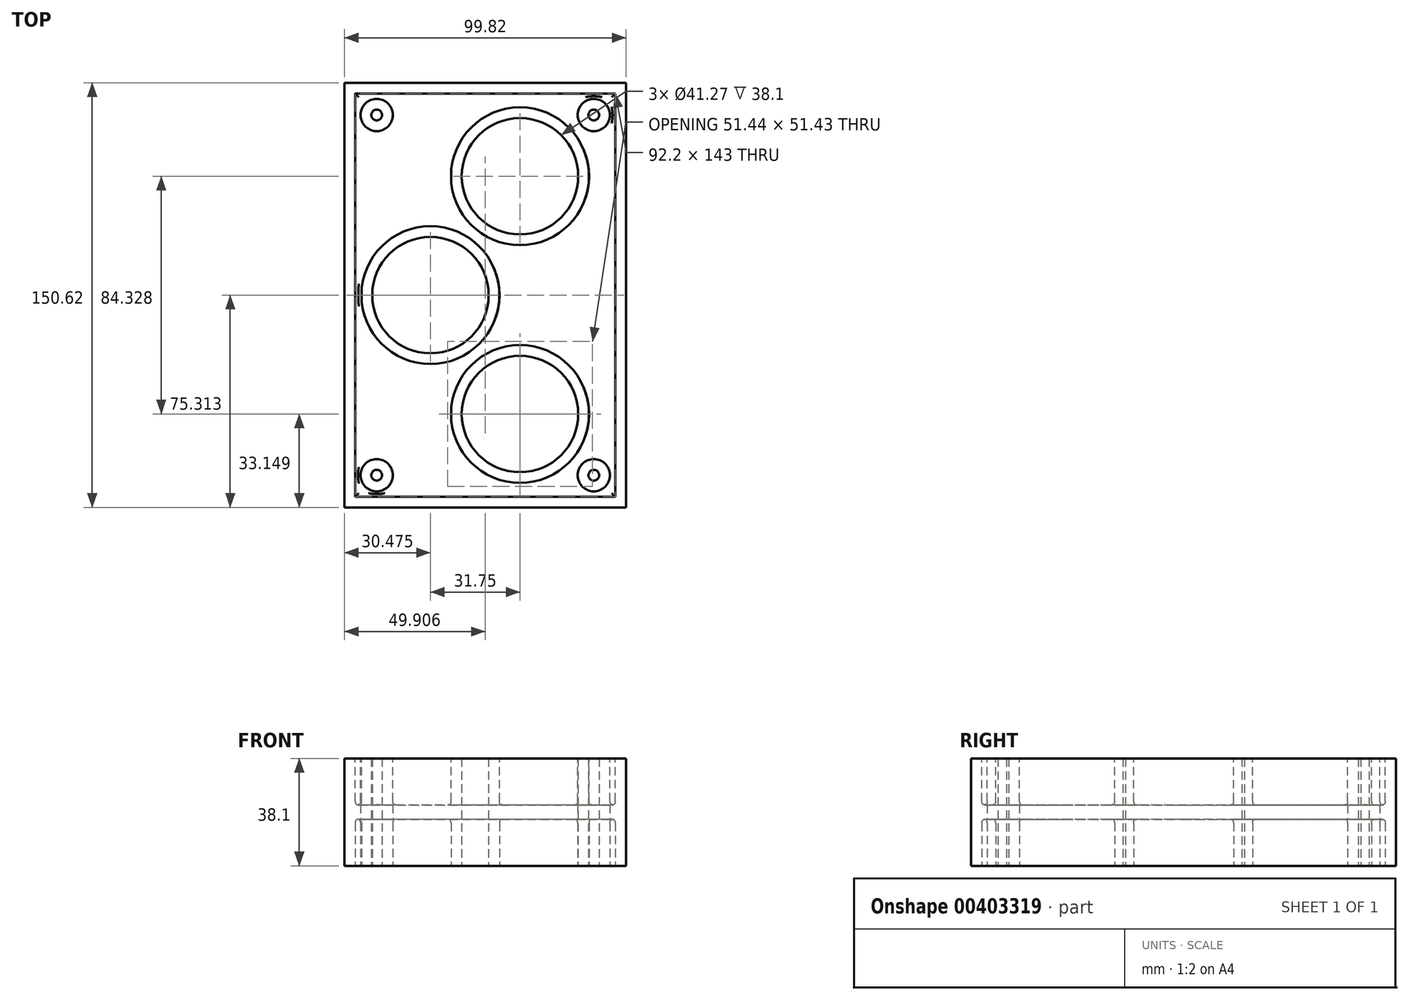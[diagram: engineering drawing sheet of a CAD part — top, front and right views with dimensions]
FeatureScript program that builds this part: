
annotation { "Feature Type Name" : "Feature", "Feature Type Description" : "" }
export const myFeature = defineFeature(function(context is Context, id is Id, definition is map)
    precondition{}
    {
        {
            var Q0;
            Q0=qCreatedBy(makeId("Top.planeOp"),FACE);
            var sketch = newSketch(context, id + "F0", { "sketchPlane" : qUnion([Q0])});
            skLineSegment(sketch, "E0.bottom", {"start": v(-39.4, 84.41) * mm, "end": v(60.42, 84.41) * mm});
            skLineSegment(sketch, "E0.top", {"start": v(-39.4, -66.2) * mm, "end": v(60.42, -66.2) * mm});
            skLineSegment(sketch, "E0.left", {"start": v(-39.4, 84.41) * mm, "end": v(-39.4, -66.2) * mm});
            skLineSegment(sketch, "E0.right", {"start": v(60.42, 84.41) * mm, "end": v(60.42, -66.2) * mm});
            skSolve(sketch);
        }
        {
            var Q0;
            Q0=makeQuery(id+"F0.imprint","IMPRINT",FACE,{"disambiguationData":[TD([[makeQuery(id+"F0.imprint","IMPRINT",EDGE,{"derivedFrom":sQuery(id+"F0.wireOp",EDGE,"E0.bottom")}),-1.0]])]});
            var Q1;
            Q1=sQuery(id+"F0.wireOp",EDGE,"E0.bottom");
            var Q2;
            Q2=sQuery(id+"F0.wireOp",EDGE,"E0.left");
            var Q3;
            Q3=sQuery(id+"F0.wireOp",EDGE,"E0.top");
            var Q4;
            Q4=sQuery(id+"F0.wireOp",EDGE,"E0.right");
            extrude(context, id + "F1", {"entities" : qUnion([Q0]), "surfaceEntities" : qUnion([Q1, Q2, Q3, Q4]), "depth" : 19.05 * mm});
        }
        {
            var Q0;
            Q0=qCreatedBy(makeId("Top.planeOp"),FACE);
            var sketch = newSketch(context, id + "F2", { "sketchPlane" : qUnion([Q0])});
            skCircle(sketch, "E1", {"center": v(22.83, 51.27) * mm, "radius": 20.64 * mm});
            skCircle(sketch, "E2", {"center": v(-8.92, 9.1) * mm, "radius": 20.64 * mm});
            skCircle(sketch, "E3", {"center": v(22.83, -33.06) * mm, "radius": 20.64 * mm});
            skLineSegment(sketch, "E4.0", {"start": v(-35.6, 80.6) * mm, "end": v(56.6, 80.6) * mm});
            skLineSegment(sketch, "E5.0", {"start": v(-35.6, 80.6) * mm, "end": v(-35.6, -62.4) * mm});
            skLineSegment(sketch, "E6.0", {"start": v(-35.6, -62.4) * mm, "end": v(56.6, -62.4) * mm});
            skLineSegment(sketch, "E7.0", {"start": v(56.6, 80.6) * mm, "end": v(56.6, -62.4) * mm});
            skLineSegment(sketch, "E8", {"start": v(-8.92, 80.6) * mm, "end": v(-8.92, -62.4) * mm, "construction": true});
            skLineSegment(sketch, "E9", {"start": v(-35.6, 9.1) * mm, "end": v(56.6, 9.1) * mm, "construction": true});
            skCircle(sketch, "E10.0", {"center": v(-8.92, 9.1) * mm, "radius": 24.45 * mm});
            skCircle(sketch, "E11.0", {"center": v(22.83, -33.06) * mm, "radius": 24.45 * mm});
            skCircle(sketch, "E12.0", {"center": v(22.83, 51.27) * mm, "radius": 24.45 * mm});
            skCircle(sketch, "E13", {"center": v(48.99, 72.98) * mm, "radius": 1.9 * mm});
            skCircle(sketch, "E14.0", {"center": v(48.99, 72.98) * mm, "radius": 5.71 * mm});
            skCircle(sketch, "E15.MirrorC", {"center": v(48.99, -54.78) * mm, "radius": 5.71 * mm});
            skLineSegment(sketch, "E16", {"start": v(10.5, 80.6) * mm, "end": v(10.5, -62.4) * mm, "construction": true});
            skCircle(sketch, "E17.MirrorC", {"center": v(48.99, -54.78) * mm, "radius": 1.9 * mm});
            skCircle(sketch, "E18.MirrorC", {"center": v(-27.97, -54.78) * mm, "radius": 5.71 * mm});
            skCircle(sketch, "E19.MirrorC", {"center": v(-27.97, -54.78) * mm, "radius": 1.9 * mm});
            skCircle(sketch, "E20.MirrorC", {"center": v(-27.97, 72.98) * mm, "radius": 5.71 * mm});
            skCircle(sketch, "E21.MirrorC", {"center": v(-27.97, 72.98) * mm, "radius": 1.9 * mm});
            skLineSegment(sketch, "E22", {"start": v(22.83, 80.6) * mm, "end": v(22.83, -62.4) * mm, "construction": true});
            skSolve(sketch);
        }
        {
            var Q0;
            Q0=makeQuery(id+"F2.imprint","IMPRINT",FACE,{"disambiguationData":[TD([[makeQuery(id+"F2.imprint","IMPRINT",EDGE,{"derivedFrom":sQuery(id+"F2.wireOp",EDGE,"E2")}),1.0]])]});
            var Q1;
            Q1=makeQuery(id+"F2.imprint","IMPRINT",FACE,{"disambiguationData":[TD([[makeQuery(id+"F2.imprint","IMPRINT",EDGE,{"derivedFrom":sQuery(id+"F2.wireOp",EDGE,"E3")}),1.0]])]});
            var Q2;
            Q2=makeQuery(id+"F2.imprint","IMPRINT",FACE,{"disambiguationData":[TD([[makeQuery(id+"F2.imprint","IMPRINT",EDGE,{"derivedFrom":sQuery(id+"F2.wireOp",EDGE,"E1")}),1.0]])]});
            var Q3;
            Q3=makeQuery(id+"F2.imprint","IMPRINT",FACE,{"disambiguationData":[TD([[makeQuery(id+"F2.imprint","IMPRINT",EDGE,{"derivedFrom":sQuery(id+"F2.wireOp",EDGE,"E21.MirrorC")}),-1.0]])]});
            var Q4;
            Q4=makeQuery(id+"F2.imprint","IMPRINT",FACE,{"disambiguationData":[TD([[makeQuery(id+"F2.imprint","IMPRINT",EDGE,{"derivedFrom":sQuery(id+"F2.wireOp",EDGE,"E17.MirrorC")}),-1.0]])]});
            var Q5;
            Q5=makeQuery(id+"F2.imprint","IMPRINT",FACE,{"disambiguationData":[TD([[makeQuery(id+"F2.imprint","IMPRINT",EDGE,{"derivedFrom":sQuery(id+"F2.wireOp",EDGE,"E19.MirrorC")}),1.0]])]});
            var Q6;
            Q6=makeQuery(id+"F2.imprint","IMPRINT",FACE,{"disambiguationData":[TD([[makeQuery(id+"F2.imprint","IMPRINT",EDGE,{"derivedFrom":sQuery(id+"F2.wireOp",EDGE,"E13")}),1.0]])]});
            extrude(context, id + "F3", {"entities" : qUnion([Q0, Q1, Q2, Q3, Q4, Q5, Q6]), "operationType" : NewBodyOperationType.REMOVE, "endBound" : BoundingType.UP_TO_NEXT, "depth" : 97.8 * mm});
        }
        {
            var Q0;
            Q0 = qSketchRegion(id + "F2", true);
            var Q1;
            Q1=makeQuery(id+"F1.opExtrude","CAP_FACE",FACE,{"disambiguationData":[OSD([sQuery(id+"F0.wireOp",EDGE,"E0.bottom"),sQuery(id+"F0.wireOp",EDGE,"E0.top"),sQuery(id+"F0.wireOp",EDGE,"E0.left"),sQuery(id+"F0.wireOp",EDGE,"E0.right")])],"isStart":false});
            extrude(context, id + "F4", {"entities" : qUnion([Q0, Q1]), "operationType" : NewBodyOperationType.REMOVE, "depth" : 16.5 * mm});
        }
        {
            var Q0;
            Q0=makeQuery(id+"F4.boolean.opBoolean","COPY",EDGE,{"derivedFrom":makeQuery(id+"F4.opExtrude","CAP_EDGE",EDGE,{"disambiguationData":[OSD([sQuery(id+"F2.wireOp",EDGE,"E10.0")])],"isStart":false})});
            var Q1;
            Q1=makeQuery(id+"F4.boolean.opBoolean","COPY",EDGE,{"derivedFrom":makeQuery(id+"F4.opExtrude","CAP_EDGE",EDGE,{"disambiguationData":[OSD([sQuery(id+"F2.wireOp",EDGE,"E18.MirrorC")])],"isStart":false})});
            var Q2;
            Q2=makeQuery(id+"F4.boolean.opBoolean","COPY",EDGE,{"derivedFrom":makeQuery(id+"F4.opExtrude","CAP_EDGE",EDGE,{"disambiguationData":[OSD([sQuery(id+"F2.wireOp",EDGE,"E5.0")])],"isStart":false})});
            var Q3;
            Q3=makeQuery(id+"F4.boolean.opBoolean","COPY",EDGE,{"derivedFrom":makeQuery(id+"F4.opExtrude","CAP_EDGE",EDGE,{"disambiguationData":[OSD([sQuery(id+"F2.wireOp",EDGE,"E6.0")])],"isStart":false})});
            var Q4;
            Q4=makeQuery(id+"F4.boolean.opBoolean","COPY",EDGE,{"derivedFrom":makeQuery(id+"F4.opExtrude","CAP_EDGE",EDGE,{"disambiguationData":[OSD([sQuery(id+"F2.wireOp",EDGE,"E4.0")])],"isStart":false})});
            var Q5;
            Q5=makeQuery(id+"F4.boolean.opBoolean","COPY",EDGE,{"derivedFrom":makeQuery(id+"F4.opExtrude","CAP_EDGE",EDGE,{"disambiguationData":[OSD([sQuery(id+"F2.wireOp",EDGE,"E20.MirrorC")])],"isStart":false})});
            var Q6;
            Q6=makeQuery(id+"F4.boolean.opBoolean","COPY",EDGE,{"derivedFrom":makeQuery(id+"F4.opExtrude","CAP_EDGE",EDGE,{"disambiguationData":[OSD([sQuery(id+"F2.wireOp",EDGE,"E14.0")])],"isStart":false})});
            var Q7;
            Q7=makeQuery(id+"F4.boolean.opBoolean","COPY",EDGE,{"derivedFrom":makeQuery(id+"F4.opExtrude","CAP_EDGE",EDGE,{"disambiguationData":[OSD([sQuery(id+"F2.wireOp",EDGE,"E15.MirrorC")])],"isStart":false})});
            var Q8;
            Q8=makeQuery(id+"F4.boolean.opBoolean","COPY",EDGE,{"derivedFrom":makeQuery(id+"F4.opExtrude","CAP_EDGE",EDGE,{"disambiguationData":[OSD([sQuery(id+"F2.wireOp",EDGE,"E7.0")])],"isStart":false})});
            var Q9;
            Q9=makeQuery(id+"F4.boolean.opBoolean","COPY",EDGE,{"derivedFrom":makeQuery(id+"F4.opExtrude","CAP_EDGE",EDGE,{"disambiguationData":[OSD([sQuery(id+"F2.wireOp",EDGE,"E11.0")])],"isStart":false})});
            var Q10;
            Q10=makeQuery(id+"F4.boolean.opBoolean","COPY",EDGE,{"derivedFrom":makeQuery(id+"F4.opExtrude","CAP_EDGE",EDGE,{"disambiguationData":[OSD([sQuery(id+"F2.wireOp",EDGE,"E12.0")])],"isStart":false})});
            fillet(context, id + "F5", {"entities" : qUnion([Q0, Q1, Q2, Q3, Q4, Q5, Q6, Q7, Q8, Q9, Q10]), "radius" : 1.27 * mm, "tangentPropagation" : true, "rho" : 0.5, "crossSection" : FilletCrossSection.CONIC, "allowEdgeOverflow" : false});
        }
        {
            var Q0;
            Q0=makeQuery(id+"F1.opExtrude","SWEPT_BODY",BODY,{"disambiguationData":[OSD([sQuery(id+"F0.wireOp",EDGE,"E0.bottom"),sQuery(id+"F0.wireOp",EDGE,"E0.top"),sQuery(id+"F0.wireOp",EDGE,"E0.left"),sQuery(id+"F0.wireOp",EDGE,"E0.right")])]});
            var Q1;
            Q1=makeQuery(id+"F1.opExtrude","CAP_FACE",FACE,{"disambiguationData":[OSD([sQuery(id+"F0.wireOp",EDGE,"E0.bottom"),sQuery(id+"F0.wireOp",EDGE,"E0.top"),sQuery(id+"F0.wireOp",EDGE,"E0.left"),sQuery(id+"F0.wireOp",EDGE,"E0.right")])],"isStart":false});
            mirror(context, id + "F6", {"operationType" : NewBodyOperationType.ADD, "entities" : qUnion([Q0]), "mirrorPlane" : qUnion([Q1])});
        }
    });
